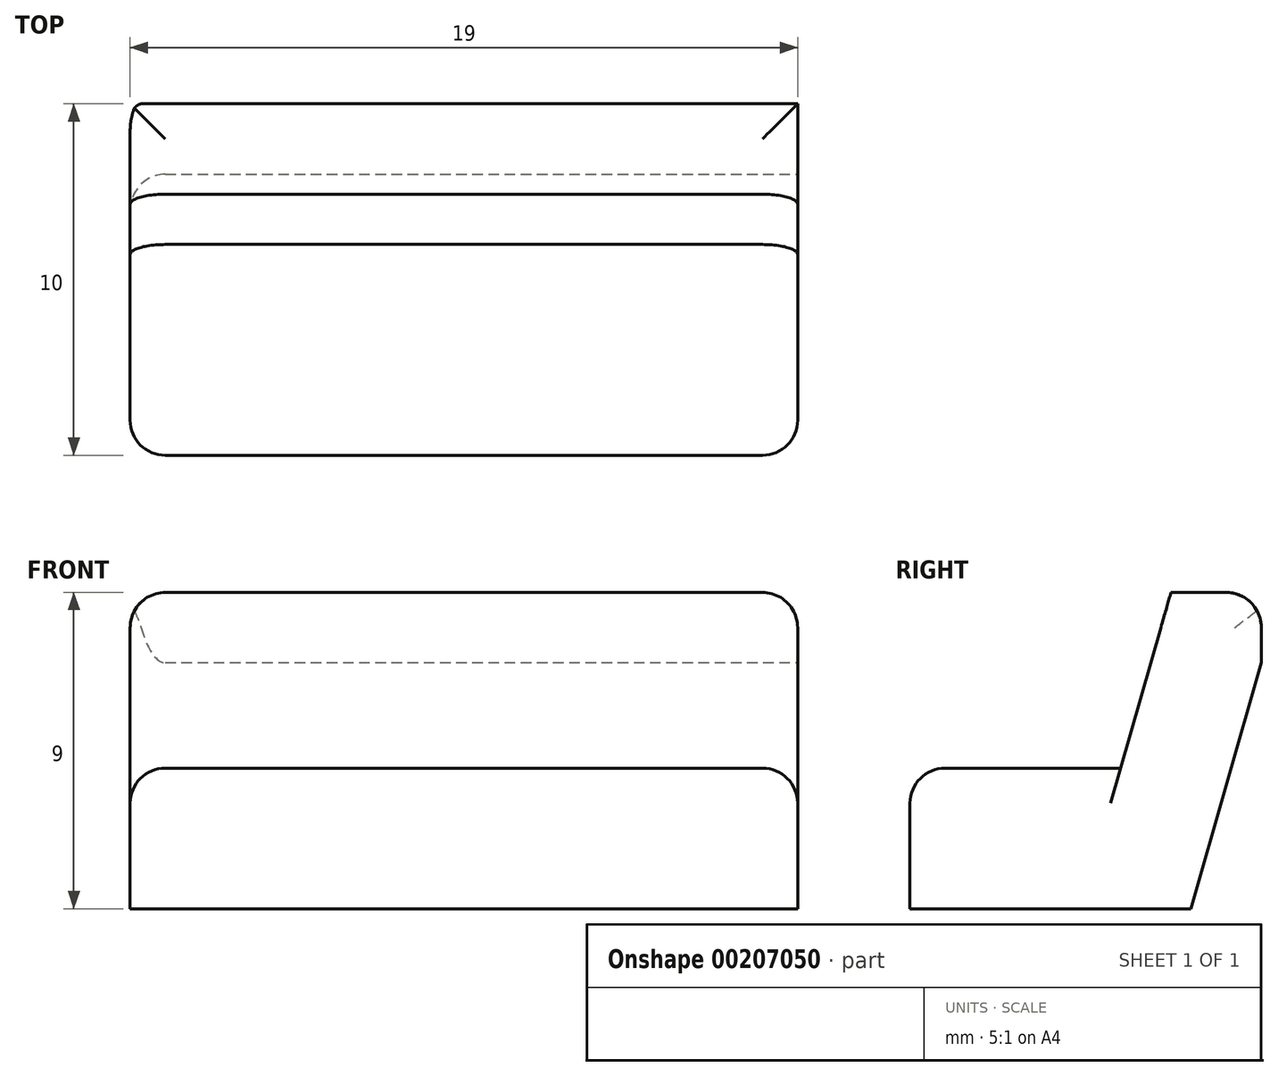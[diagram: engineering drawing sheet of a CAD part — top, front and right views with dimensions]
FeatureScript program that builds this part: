
annotation { "Feature Type Name" : "Feature", "Feature Type Description" : "" }
export const myFeature = defineFeature(function(context is Context, id is Id, definition is map)
    precondition{}
    {
        {
            var Q0;
            Q0=qCreatedBy(makeId("Top.planeOp"),FACE);
            var sketch = newSketch(context, id + "F0", { "sketchPlane" : qUnion([Q0])});
            skLineSegment(sketch, "E0.bottom", {"start": v(9.5, -5) * mm, "end": v(-9.5, -5) * mm});
            skLineSegment(sketch, "E0.top", {"start": v(9.5, 5) * mm, "end": v(-9.5, 5) * mm});
            skLineSegment(sketch, "E0.left", {"start": v(9.5, -5) * mm, "end": v(9.5, 5) * mm});
            skLineSegment(sketch, "E0.right", {"start": v(-9.5, -5) * mm, "end": v(-9.5, 5) * mm});
            skPoint(sketch, "E0.middle", {"position": v(0, 0) * mm});
            skSolve(sketch);
        }
        {
            var Q0;
            Q0=makeQuery(id+"F0.imprint","IMPRINT",FACE,{"disambiguationData":[TD([[makeQuery(id+"F0.imprint","IMPRINT",EDGE,{"derivedFrom":sQuery(id+"F0.wireOp",EDGE,"E0.bottom")}),-1.0]])]});
            extrude(context, id + "F1", {"entities" : qUnion([Q0]), "depth" : 4 * mm});
        }
        {
            var Q0;
            Q0=makeQuery(id+"F1.opExtrude","CAP_FACE",FACE,{"disambiguationData":[OSD([sQuery(id+"F0.wireOp",EDGE,"E0.bottom"),sQuery(id+"F0.wireOp",EDGE,"E0.top"),sQuery(id+"F0.wireOp",EDGE,"E0.left"),sQuery(id+"F0.wireOp",EDGE,"E0.right")])],"isStart":false});
            var sketch = newSketch(context, id + "F2", { "sketchPlane" : qUnion([Q0])});
            skLineSegment(sketch, "E1.bottom", {"start": v(-9.5, 5) * mm, "end": v(9.5, 5) * mm});
            skLineSegment(sketch, "E1.top", {"start": v(-9.5, 1) * mm, "end": v(9.5, 1) * mm});
            skLineSegment(sketch, "E1.left", {"start": v(-9.5, 5) * mm, "end": v(-9.5, 1) * mm});
            skLineSegment(sketch, "E1.right", {"start": v(9.5, 5) * mm, "end": v(9.5, 1) * mm});
            skSolve(sketch);
        }
        {
            var Q0;
            Q0=makeQuery(id+"F2.imprint","IMPRINT",FACE,{"disambiguationData":[TD([[makeQuery(id+"F2.imprint","IMPRINT",EDGE,{"derivedFrom":sQuery(id+"F2.wireOp",EDGE,"E1.bottom")}),1.0]])]});
            extrude(context, id + "F3", {"entities" : qUnion([Q0]), "operationType" : NewBodyOperationType.ADD, "depth" : 5 * mm});
        }
        {
            var Q0;
            Q0=makeQuery(id+"F3.boolean.opBoolean","MERGE",FACE,{"derivedFrom":[makeQuery(id+"F1.opExtrude","SWEPT_FACE",FACE,{"disambiguationData":[OSD([sQuery(id+"F0.wireOp",EDGE,"E0.left")])]}),makeQuery(id+"F3.opExtrude","SWEPT_FACE",FACE,{"disambiguationData":[OSD([sQuery(id+"F2.wireOp",EDGE,"E1.right")])]})]});
            var sketch = newSketch(context, id + "F4", { "sketchPlane" : qUnion([Q0])});
            skLineSegment(sketch, "E2", {"start": v(5, 7) * mm, "end": v(3, 0) * mm});
            skLineSegment(sketch, "E3", {"start": v(1, 4) * mm, "end": v(2.43, 9) * mm});
            skSolve(sketch);
        }
        {
            var Q0;
            {var subQ0=sQuery(id+"F4.wireOp",EDGE,"E2");Q0=makeQuery(id+"F4.imprint","IMPRINT",FACE,{"disambiguationData":[TD([[makeQuery(id+"F4.imprint","IMPRINT",EDGE,{"derivedFrom":subQ0}),1.0]])]});}
            var Q1;
            {var subQ0=sQuery(id+"F4.wireOp",EDGE,"E3");Q1=makeQuery(id+"F4.imprint","IMPRINT",FACE,{"disambiguationData":[TD([[makeQuery(id+"F4.imprint","IMPRINT",EDGE,{"derivedFrom":subQ0}),1.0]])]});}
            extrude(context, id + "F5", {"entities" : qUnion([Q0, Q1]), "operationType" : NewBodyOperationType.REMOVE, "endBound" : BoundingType.THROUGH_ALL, "oppositeDirection" : true, "depth" : 25 * mm});
        }
        {
            var Q0;
            Q0=makeQuery(id+"F3.opExtrude","CAP_EDGE",EDGE,{"disambiguationData":[OSD([sQuery(id+"F2.wireOp",EDGE,"E1.bottom")])],"isStart":false});
            var Q1;
            Q1=makeQuery(id+"F3.opExtrude","CAP_EDGE",EDGE,{"disambiguationData":[OSD([sQuery(id+"F2.wireOp",EDGE,"E1.top")])],"isStart":false});
            var Q2;
            Q2=makeQuery(id+"F1.opExtrude","CAP_EDGE",EDGE,{"disambiguationData":[OSD([sQuery(id+"F0.wireOp",EDGE,"E0.bottom")])],"isStart":false});
            var Q3;
            Q3=makeQuery(id+"F3.opExtrude","CAP_EDGE",EDGE,{"disambiguationData":[OSD([sQuery(id+"F2.wireOp",EDGE,"E1.top")])],"isStart":true});
            var Q4;
            Q4=makeQuery(id+"F5.boolean.opBoolean","COPY",EDGE,{"derivedFrom":makeQuery(id+"F5.opExtrude","SWEPT_EDGE",EDGE,{"disambiguationData":[OSD([sQuery(id+"F0.wireOp",EDGE,"E0.top"),sQuery(id+"F0.wireOp",EDGE,"E0.left"),sQuery(id+"F2.wireOp",EDGE,"E1.bottom"),sQuery(id+"F2.wireOp",EDGE,"E1.right"),sQuery(id+"F4.wireOp",EDGE,"E2")])]})});
            var Q5;
            Q5=makeQuery(id+"F5.boolean.opBoolean","COPY",EDGE,{"derivedFrom":makeQuery(id+"F5.opExtrude","SWEPT_EDGE",EDGE,{"disambiguationData":[OSD([sQuery(id+"F2.wireOp",EDGE,"E1.right"),sQuery(id+"F4.wireOp",EDGE,"E3")])]})});
            var Q6;
            Q6=makeQuery(id+"F1.opExtrude","CAP_EDGE",EDGE,{"disambiguationData":[OSD([sQuery(id+"F0.wireOp",EDGE,"E0.left")])],"isStart":false});
            var Q7;
            Q7=makeQuery(id+"F1.opExtrude","CAP_EDGE",EDGE,{"disambiguationData":[OSD([sQuery(id+"F0.wireOp",EDGE,"E0.right")])],"isStart":false});
            var Q8;
            Q8=makeQuery(id+"F3.opExtrude","CAP_EDGE",EDGE,{"disambiguationData":[OSD([sQuery(id+"F2.wireOp",EDGE,"E1.right")])],"isStart":false});
            var Q9;
            Q9=makeQuery(id+"F3.opExtrude","CAP_EDGE",EDGE,{"disambiguationData":[OSD([sQuery(id+"F2.wireOp",EDGE,"E1.left")])],"isStart":false});
            var Q10;
            Q10=makeQuery(id+"F1.opExtrude","SWEPT_EDGE",EDGE,{"disambiguationData":[OSD([sQuery(id+"F0.wireOp",EDGE,"E0.bottom"),sQuery(id+"F0.wireOp",EDGE,"E0.left")])]});
            var Q11;
            Q11=makeQuery(id+"F1.opExtrude","SWEPT_EDGE",EDGE,{"disambiguationData":[OSD([sQuery(id+"F0.wireOp",EDGE,"E0.bottom"),sQuery(id+"F0.wireOp",EDGE,"E0.right")])]});
            var Q12;
            Q12=makeQuery(id+"F5.boolean.opBoolean","COPY",EDGE,{"derivedFrom":makeQuery(id+"F5.opExtrude","CAP_EDGE",EDGE,{"disambiguationData":[OSD([sQuery(id+"F4.wireOp",EDGE,"E2")])],"isStart":true})});
            var Q13;
            Q13=makeQuery(id+"F5.boolean.opBoolean","INTERSECT",EDGE,{"derivedFrom":[makeQuery(id+"F3.boolean.opBoolean","MERGE",FACE,{"derivedFrom":[makeQuery(id+"F1.opExtrude","SWEPT_FACE",FACE,{"disambiguationData":[OSD([sQuery(id+"F0.wireOp",EDGE,"E0.right")])]}),makeQuery(id+"F3.opExtrude","SWEPT_FACE",FACE,{"disambiguationData":[OSD([sQuery(id+"F2.wireOp",EDGE,"E1.left")])]})]}),makeQuery(id+"F5.opExtrude","SWEPT_FACE",FACE,{"disambiguationData":[OSD([sQuery(id+"F4.wireOp",EDGE,"E2")])]})]});
            fillet(context, id + "F6", {"entities" : qUnion([Q0, Q1, Q2, Q3, Q4, Q5, Q6, Q7, Q8, Q9, Q10, Q11, Q12, Q13]), "radius" : 1 * mm, "tangentPropagation" : true, "allowEdgeOverflow" : false});
        }
    });
